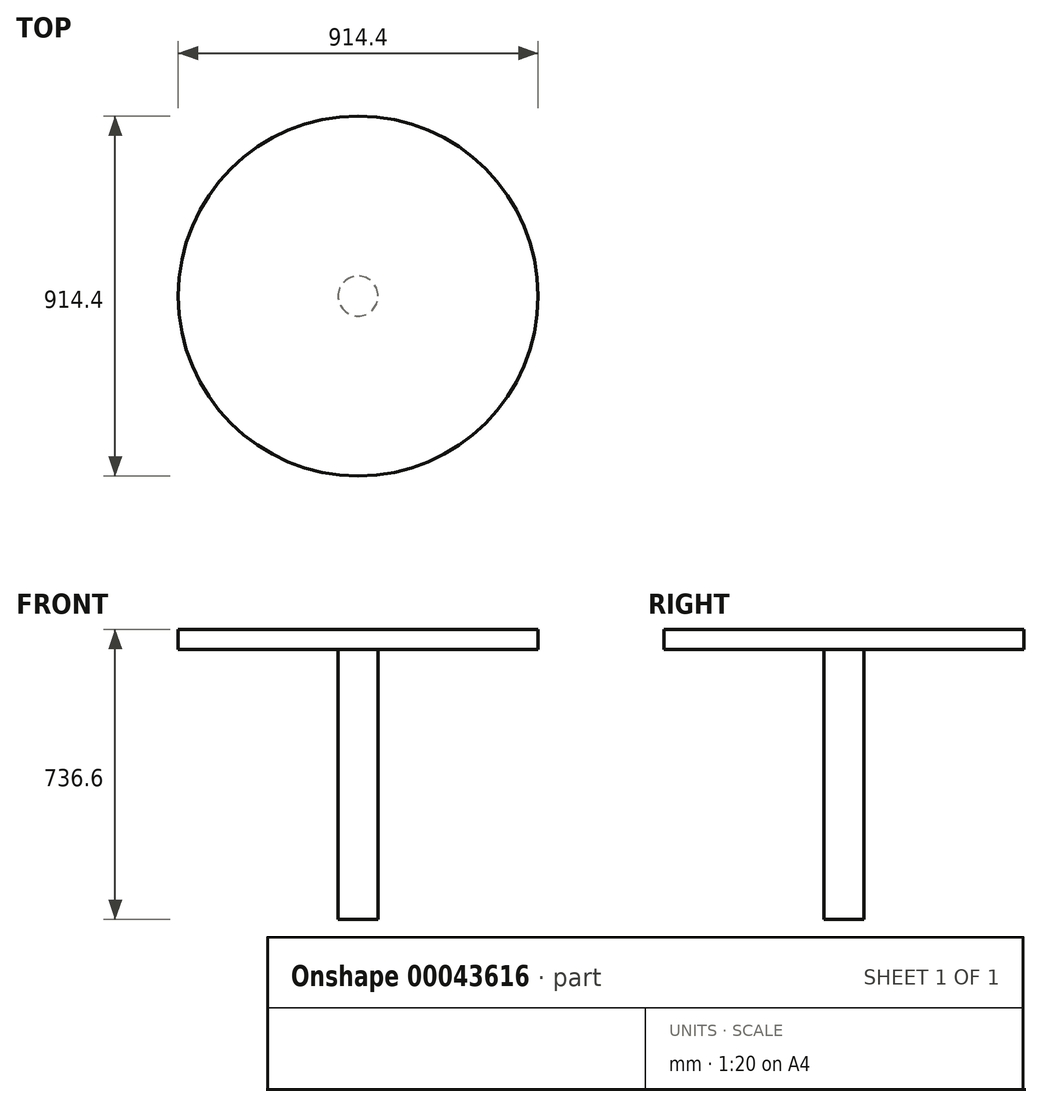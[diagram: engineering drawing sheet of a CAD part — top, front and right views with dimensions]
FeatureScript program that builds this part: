
annotation { "Feature Type Name" : "Feature", "Feature Type Description" : "" }
export const myFeature = defineFeature(function(context is Context, id is Id, definition is map)
    precondition{}
    {
        {
            var Q0;
            Q0=qCreatedBy(makeId("Top.planeOp"),FACE);
            var sketch = newSketch(context, id + "F0", { "sketchPlane" : qUnion([Q0])});
            skCircle(sketch, "E0", {"center": v(0, 0) * mm, "radius": 457.2 * mm});
            skSolve(sketch);
        }
        {
            var Q0;
            Q0=makeQuery(id+"F0.imprint","IMPRINT",FACE,{"disambiguationData":[TD([[makeQuery(id+"F0.imprint","IMPRINT",EDGE,{"derivedFrom":sQuery(id+"F0.wireOp",EDGE,"E0")}),1.0]])]});
            extrude(context, id + "F1", {"entities" : qUnion([Q0]), "oppositeDirection" : true, "depth" : 50.8 * mm});
        }
        {
            var Q0;
            Q0=makeQuery(id+"F1.opExtrude","CAP_FACE",FACE,{"disambiguationData":[OSD([sQuery(id+"F0.wireOp",EDGE,"E0")])],"isStart":true});
            var sketch = newSketch(context, id + "F2", { "sketchPlane" : qUnion([Q0])});
            skCircle(sketch, "E1", {"center": v(0, 0) * mm, "radius": 50.8 * mm});
            skSolve(sketch);
        }
        {
            var Q0;
            Q0=makeQuery(id+"F2.imprint","IMPRINT",FACE,{"disambiguationData":[TD([[makeQuery(id+"F2.imprint","IMPRINT",EDGE,{"derivedFrom":sQuery(id+"F2.wireOp",EDGE,"E1")}),1.0]])]});
            extrude(context, id + "F3", {"entities" : qUnion([Q0]), "operationType" : NewBodyOperationType.ADD, "oppositeDirection" : true, "depth" : 736.6 * mm});
        }
    });
